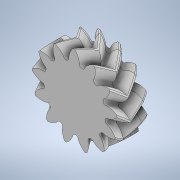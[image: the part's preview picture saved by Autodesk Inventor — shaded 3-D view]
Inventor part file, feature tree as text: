
AUTODESK INVENTOR PART (.ipt)
format: ipt  version: 2022 (Build 260153070, 153G)  size: 1,163,264 bytes
history: native  units: mm
features: sketch x2, helix x2, extrude x1, pattern_circular x1, mirror x1, projected_geometry x1
ambient origin geometry x8: Origin, YZ Plane, XZ Plane, XY Plane, X Axis, Y Axis, Z Axis, Center Point
bodies: Solid1 (feature_tree)
feature tree (8):
  sketch  "Sketch1"  dims[d0=1.5mm d1=0.0mm]
  extrude  "Extrusion1"  TaperAngle=0.0deg  [1 undecoded]
  helix  "Coil1"  [1 undecoded]
  pattern_circular  "Circular Pattern1"  [2 undecoded]
  mirror  "Mirror1"
  helix  "Coil2"  [1 undecoded]
  sketch  "Sketch2"  dims[d2=1.5mm d3=1.5mm d4=0.416667mm d5=0.0mm d6=90.0deg d7=90.0deg d8=0.0mm d9=0.0mm d10=130.0mm d11=360.0deg d14=1.5mm d15=0.5mm d16=0.208333mm d17=0.0mm d18=90.0deg d19=90.0deg d20=0.0mm d21=0.0mm]
  projected_geometry  "Projected Loop1"
note: 5 required parameter values undecoded (feature->parameter linkage not recoverable at this tier; creation-order binding heuristic only, values carry confidence <= 0.55)
